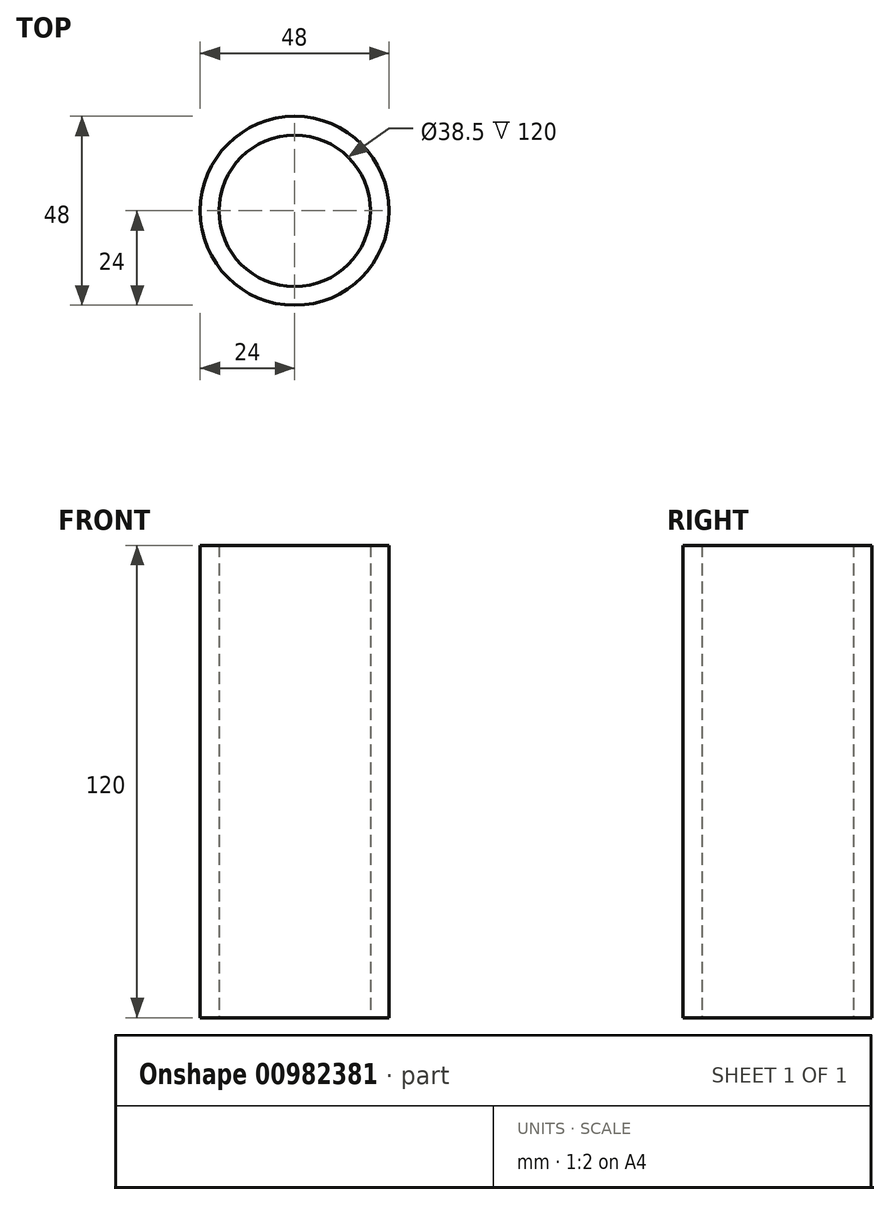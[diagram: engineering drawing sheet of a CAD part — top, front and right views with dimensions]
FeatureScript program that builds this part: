
annotation { "Feature Type Name" : "Feature", "Feature Type Description" : "" }
export const myFeature = defineFeature(function(context is Context, id is Id, definition is map)
    precondition{}
    {
        {
            var Q0;
            Q0=qCreatedBy(makeId("Top.planeOp"),FACE);
            var sketch = newSketch(context, id + "F0", { "sketchPlane" : qUnion([Q0])});
            skCircle(sketch, "E0", {"center": v(0, 0) * mm, "radius": 19.25 * mm});
            skCircle(sketch, "E1", {"center": v(0, 0) * mm, "radius": 24 * mm});
            skSolve(sketch);
        }
        {
            var Q0;
            Q0=makeQuery(id+"F0.imprint","IMPRINT",FACE,{"disambiguationData":[TD([[makeQuery(id+"F0.imprint","IMPRINT",EDGE,{"derivedFrom":sQuery(id+"F0.wireOp",EDGE,"E0")}),-1.0]])]});
            extrude(context, id + "F1", {"entities" : qUnion([Q0]), "depth" : 120 * mm, "offsetDistance" : 25 * mm});
        }
    });
